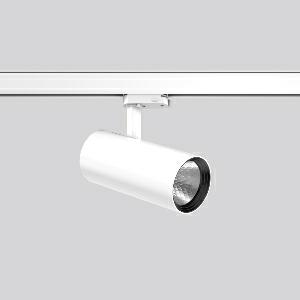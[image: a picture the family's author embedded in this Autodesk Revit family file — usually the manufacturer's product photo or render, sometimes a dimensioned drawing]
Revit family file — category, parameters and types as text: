
# Revit family: deecos_s_mini_742193_002_1_76_f4d5
name_source: partatom
category: Lighting Fixtures
units: mm (PartAtom-declared; Revit-internal decimal feet)

## family parameters
Cut with Voids When Loaded = No
Host = Face
Light Source = No
Part Type = Normal
Room Calculation Point = No
Round Connector Dimension = Use Diameter
Shared = No

## types (1)
- DEECOS S mini (1 x LED Modul 940, 2500 lm, 4000)
    Apparent Load = 22 VA
    Approval mark = CE
    CIE Flux Codes = 100 100 100 100 100
    Color Rendering = 92
    Color Temperature = 4000
    Default Elevation = 1800 mm
    Description = Series: DEECOS S mini
LED surface-mounted projector in modern design with no visible cooling ribs. Housing: die-cast aluminium, powder-coated. Rotation range: 356°. Swivel range: 90°. Black plastic ring and recessed LED to prevent glare from the side. Optical assembly with reflector made of MIRO-Silver with 98% total light reflection for outstanding efficiency - can be changed without tools. Best colour rendering index Ra>90. Superspot version with small spot LED. With adapter for RZB 3-circuit DALI tracks. Suitable for Track on ceiling, Wall track. High quality converter without flickering and stroboscopic effect. The following accessories can be mounted without use of tools: interchangeable lenses, decorative glasses, honeycomb louvre, clear and frosted diffusers, white interchangeable plastic ring. 
Colour: traffic white, matt (RAL 9016)
Diameter: 87 mm
Height: 214 mm
Lamp: LED
Socket: without socket
Colour temperature: 4000K
Colour rendering index (CRI): 92
System power: 22 W
Rated luminous flux: 2500 lm
Luminous efficiency: 114 lm/W
Control gear: Converter, dimmable, DALI
Protection class: I
Type of protection: IP 20
    Height = 214 mm
    Lamp = 1 x LED Modul 940
    Lamp Light Flux = 2500 lm
    Lamp count = 1
    Length = 87 mm
    Lifetime = 50000 h
    Luminous efficacy = 114 lm/W
    Manufacturer = RZB
    ModVariant = No
    Model = 742193.002.1.76
    Mounting Place = Ceiling
    Mounting Type = Rail mounted
    Number of Poles = 1
    OnlyDefault = Yes
    Power Factor = 1
    Product Name = DEECOS S mini
    Product group = Track mounted projectors
    ProductGroupID = 301
    Protection Class = Protection class I
    Protection Degree = IP 20
    RLX_Detail_Level = 1
    RLX_Emergency_Light_Flux = 0 lm
    RLX_Emergency_Type = 0
    RLX_Emergency_Type_DB = No
    RlxData = <blob elided: 35341 chars, md5=4d651f95>
    Socket = socket
    Standby Power = 0 W
    System Light Flux = 2500 lm
    System Power = 22 W
    Type Comments = Product without accessories
    Type Image = 741926.002.jpg
    URL = http://relux.com
    VarID = ---
    Voltage = 230 V
    Voltage Range = 220-240 V
    Weight = 0.00 kg
    Width = 0 mm  [stored 0 ft]

note: [stored X ft] marks values corroborated as IEEE doubles in the binary element streams (Revit-internal decimal feet)

## geometry (parser evidence)
native form markers: Blend x4, Sweep x11
no freeform markers — native parametric forms only
